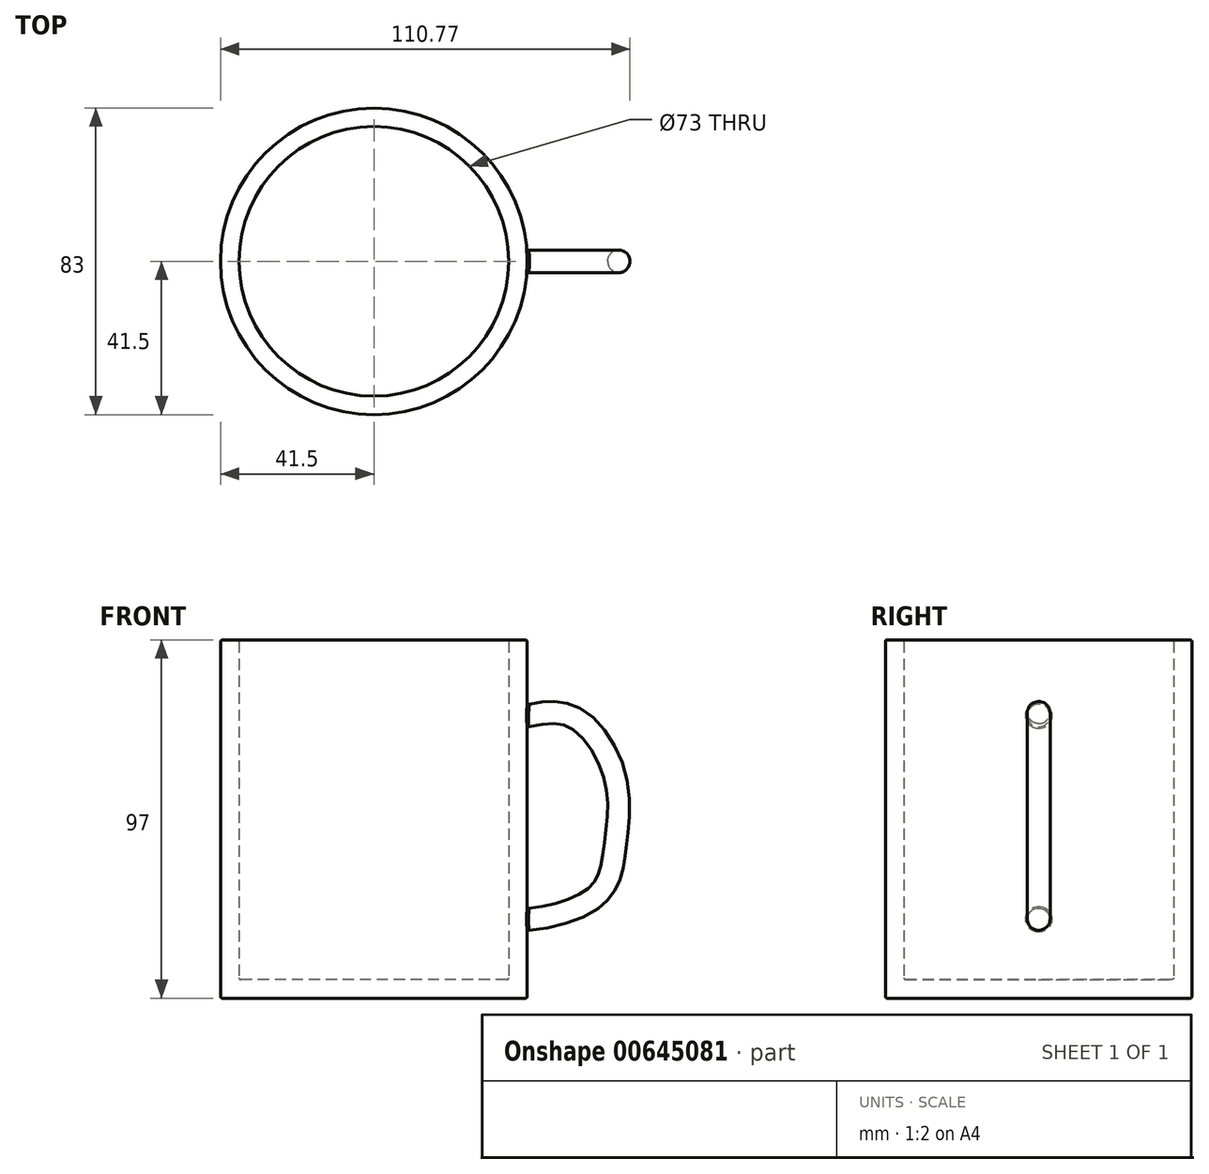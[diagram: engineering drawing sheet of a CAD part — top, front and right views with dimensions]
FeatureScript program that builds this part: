
annotation { "Feature Type Name" : "Feature", "Feature Type Description" : "" }
export const myFeature = defineFeature(function(context is Context, id is Id, definition is map)
    precondition{}
    {
        {
            var Q0;
            Q0=qCreatedBy(makeId("Top.planeOp"),FACE);
            var sketch = newSketch(context, id + "F0", { "sketchPlane" : qUnion([Q0])});
            skCircle(sketch, "E0", {"center": v(0, 0) * mm, "radius": 41.5 * mm});
            skSolve(sketch);
        }
        {
            var Q0;
            Q0 = qSketchRegion(id + "F0", true);
            extrude(context, id + "F1", {"entities" : qUnion([Q0]), "depth" : 97 * mm, "offsetDistance" : 25 * mm});
        }
        {
            var Q0;
            Q0=qCreatedBy(makeId("Front.planeOp"),FACE);
            var sketch = newSketch(context, id + "F2", { "sketchPlane" : qUnion([Q0])});
            skFitSpline(sketch, "E1", {"points": [v(36.15, 75.67) * mm, v(54.15, 76.69) * mm, v(66.03, 59.37) * mm, v(66.03, 42.06) * mm, v(62.63, 29.5) * mm, v(50.75, 22.37) * mm, v(34.46, 22.03) * mm, v(25.97, 32.9) * mm], "startDerivative": vector(125.89, 35) * mm, "endDerivative": vector(-50.94, 101.03) * mm});
            skSolve(sketch);
        }
        {
            var Q0;
            Q0=qCreatedBy(makeId("Right.planeOp"),FACE);
            cPlane(context, id + "F3", {"entities" : qUnion([Q0]), "cplaneType" : CPlaneType.OFFSET, "offset" : 41.5 * mm, "width" : 150 * mm, "height" : 150 * mm});
        }
        {
            var Q0;
            Q0=qCreatedBy(id+"F3.planeOp",FACE);
            var sketch = newSketch(context, id + "F4", { "sketchPlane" : qUnion([Q0])});
            skCircle(sketch, "E2", {"center": v(0, 76.44) * mm, "radius": 3.07 * mm});
            skSolve(sketch);
        }
        {
            var Q0;
            Q0=makeQuery(id+"F4.imprint","IMPRINT",FACE,{"disambiguationData":[TD([[makeQuery(id+"F4.imprint","IMPRINT",EDGE,{"derivedFrom":sQuery(id+"F4.wireOp",EDGE,"E2")}),1.0]])]});
            var Q1;
            Q1 = qConstructionFilter(qBodyType(qCreatedBy(id + "F2" ,EDGE), BodyType.WIRE), ConstructionObject.NO);
            sweep(context, id + "F5", {"operationType" : NewBodyOperationType.ADD, "profiles" : qUnion([Q0]), "path" : qUnion([Q1])});
        }
        {
            var Q0;
            Q0=makeQuery(id+"F1.opExtrude","CAP_FACE",FACE,{"disambiguationData":[OSD([sQuery(id+"F0.wireOp",EDGE,"E0")])],"isStart":false});
            shell(context, id + "F6", {"entities" : qUnion([Q0]), "thickness" : 5 * mm});
        }
        {
            var Q0;
            Q0=makeQuery(id+"F1.opExtrude","CAP_EDGE",EDGE,{"disambiguationData":[OSD([sQuery(id+"F0.wireOp",EDGE,"E0")])],"isStart":false});
            var Q1;
            Q1=makeQuery(id+"F5.opSweep","SWEPT_FACE",FACE,{"disambiguationData":[OSD([sQuery(id+"F2.wireOp",EDGE,"E1"),sQuery(id+"F4.wireOp",EDGE,"E2")])]});
            var Q2;
            {var subQ0=sQuery(id+"F0.wireOp",EDGE,"E0");Q2=makeQuery(id+"F6.opShell","OFFSET_EDGE",EDGE,{"disambiguationData":[OSD([subQ0]),TDD([makeQuery(id+"F1.opExtrude","CAP_EDGE",EDGE,{"disambiguationData":[OSD([subQ0])],"isStart":false})])]});}
            var Q3;
            {var subQ0=sQuery(id+"F0.wireOp",EDGE,"E0");Q3=makeQuery(id+"F6.opShell","OFFSET_EDGE",EDGE,{"disambiguationData":[OSD([subQ0]),TDD([makeQuery(id+"F1.opExtrude","CAP_EDGE",EDGE,{"disambiguationData":[OSD([subQ0])],"isStart":true})])]});}
            var Q4;
            Q4=makeQuery(id+"F1.opExtrude","CAP_EDGE",EDGE,{"disambiguationData":[OSD([sQuery(id+"F0.wireOp",EDGE,"E0")])],"isStart":true});
            fillet(context, id + "F7", {"entities" : qUnion([Q0, Q1, Q2, Q3, Q4]), "radius" : 0.5 * mm, "tangentPropagation" : true, "allowEdgeOverflow" : false});
        }
    });
